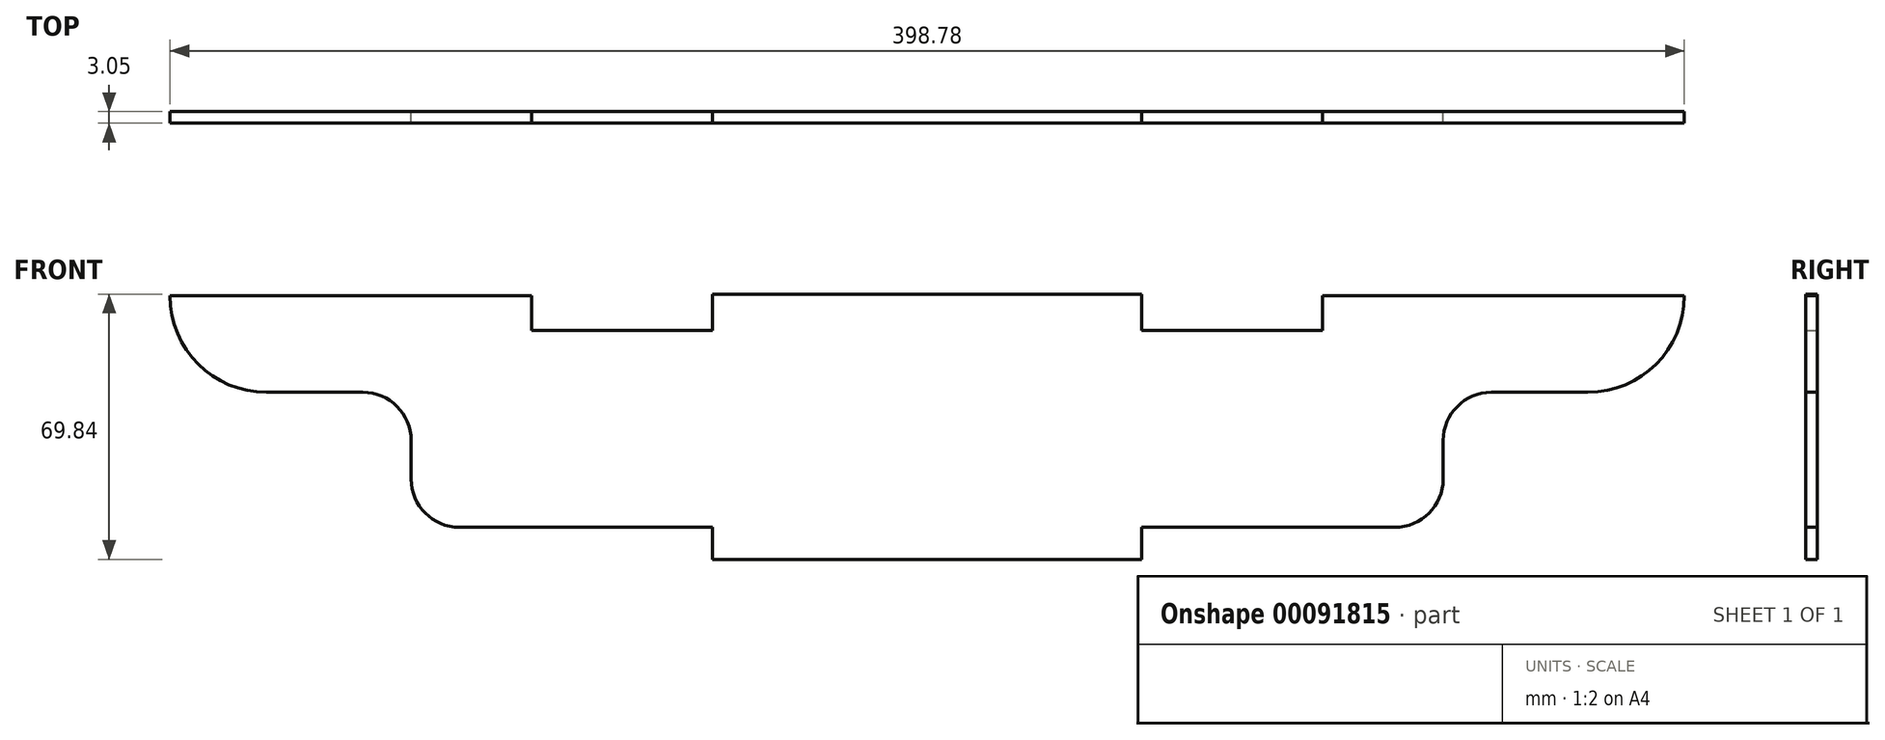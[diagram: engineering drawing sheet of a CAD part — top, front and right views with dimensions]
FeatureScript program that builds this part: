
annotation { "Feature Type Name" : "Feature", "Feature Type Description" : "" }
export const myFeature = defineFeature(function(context is Context, id is Id, definition is map)
    precondition{}
    {
        {
            var Q0;
            Q0=qCreatedBy(makeId("Front.planeOp"),FACE);
            var sketch = newSketch(context, id + "F0", { "sketchPlane" : qUnion([Q0])});
            skLineSegment(sketch, "E0.bottom", {"start": v(56.52, -34.93) * mm, "end": v(-56.52, -34.93) * mm});
            skLineSegment(sketch, "E0.top", {"start": v(56.52, 34.93) * mm, "end": v(-56.52, 34.93) * mm});
            skLineSegment(sketch, "E0.left", {"start": v(56.52, -34.92) * mm, "end": v(56.52, 34.93) * mm});
            skLineSegment(sketch, "E0.right", {"start": v(-56.52, -34.93) * mm, "end": v(-56.52, 34.93) * mm});
            skPoint(sketch, "E0.middle", {"position": v(0, 0) * mm});
            skLineSegment(sketch, "E1", {"start": v(-56.52, 34.93) * mm, "end": v(-56.52, 25.4) * mm});
            skLineSegment(sketch, "E2", {"start": v(-56.52, 25.4) * mm, "end": v(-104.14, 25.4) * mm});
            skLineSegment(sketch, "E3", {"start": v(-104.14, 25.4) * mm, "end": v(-104.14, 34.46) * mm});
            skLineSegment(sketch, "E4", {"start": v(-104.14, 34.46) * mm, "end": v(-199.4, 34.46) * mm});
            skLineSegment(sketch, "E5", {"start": v(-199.4, 34.46) * mm, "end": v(-199.4, 34.46) * mm});
            skLineSegment(sketch, "E6", {"start": v(-174, 9.06) * mm, "end": v(-148.6, 9.06) * mm});
            skLineSegment(sketch, "E7", {"start": v(-135.9, -3.64) * mm, "end": v(-135.9, -13.8) * mm});
            skLineSegment(sketch, "E8", {"start": v(-123.2, -26.5) * mm, "end": v(-56.52, -26.5) * mm});
            skLineSegment(sketch, "E9.MirrorCS", {"start": v(104.14, 25.4) * mm, "end": v(104.14, 34.46) * mm});
            skLineSegment(sketch, "E10.MirrorCS", {"start": v(56.52, 34.93) * mm, "end": v(56.52, 25.4) * mm});
            skLineSegment(sketch, "E11.MirrorCS", {"start": v(-56.52, -34.93) * mm, "end": v(56.52, -34.93) * mm});
            skLineSegment(sketch, "E12.MirrorCS", {"start": v(123.2, -26.5) * mm, "end": v(56.52, -26.5) * mm});
            skLineSegment(sketch, "E13.MirrorCS", {"start": v(135.9, -3.64) * mm, "end": v(135.9, -13.8) * mm});
            skLineSegment(sketch, "E14.MirrorCS", {"start": v(104.14, 34.46) * mm, "end": v(199.4, 34.46) * mm});
            skLineSegment(sketch, "E15.MirrorCS", {"start": v(174, 9.06) * mm, "end": v(148.6, 9.06) * mm});
            skLineSegment(sketch, "E16.MirrorCS", {"start": v(199.4, 34.46) * mm, "end": v(199.4, 34.46) * mm});
            skLineSegment(sketch, "E17.MirrorCS", {"start": v(-56.52, 34.93) * mm, "end": v(56.52, 34.93) * mm});
            skLineSegment(sketch, "E18.MirrorCS", {"start": v(56.52, 25.4) * mm, "end": v(104.14, 25.4) * mm});
            skLineSegment(sketch, "E19.MirrorCS", {"start": v(56.52, -34.93) * mm, "end": v(56.52, 34.93) * mm});
            skPoint(sketch, "E20.visualSharp", {"position": v(-199.4, 9.06) * mm});
            skArc(sketch, "E20.filletArc", {"start": v(-199.4, 34.46) * mm, "mid": v(-191.95, 16.5) * mm, "end": v(-174, 9.06) * mm});
            skPoint(sketch, "E21.visualSharp", {"position": v(199.4, 9.06) * mm});
            skArc(sketch, "E21.filletArc", {"start": v(174, 9.06) * mm, "mid": v(191.95, 16.5) * mm, "end": v(199.4, 34.46) * mm});
            skPoint(sketch, "E22.visualSharp", {"position": v(135.9, 9.06) * mm});
            skArc(sketch, "E22.filletArc", {"start": v(148.6, 9.06) * mm, "mid": v(139.6, 5.34) * mm, "end": v(135.9, -3.64) * mm});
            skPoint(sketch, "E23.visualSharp", {"position": v(135.9, -26.5) * mm});
            skArc(sketch, "E23.filletArc", {"start": v(123.2, -26.5) * mm, "mid": v(132.17, -22.78) * mm, "end": v(135.9, -13.8) * mm});
            skPoint(sketch, "E24.visualSharp", {"position": v(-135.9, -26.5) * mm});
            skArc(sketch, "E24.filletArc", {"start": v(-135.9, -13.8) * mm, "mid": v(-132.17, -22.78) * mm, "end": v(-123.2, -26.5) * mm});
            skPoint(sketch, "E25.visualSharp", {"position": v(-135.9, 9.06) * mm});
            skArc(sketch, "E25.filletArc", {"start": v(-135.9, -3.64) * mm, "mid": v(-139.6, 5.34) * mm, "end": v(-148.6, 9.06) * mm});
            skSolve(sketch);
        }
        {
            var Q0;
            Q0 = qSketchRegion(id + "F0", true);
            extrude(context, id + "F1", {"entities" : qUnion([Q0]), "depth" : 3.05 * mm});
        }
    });
